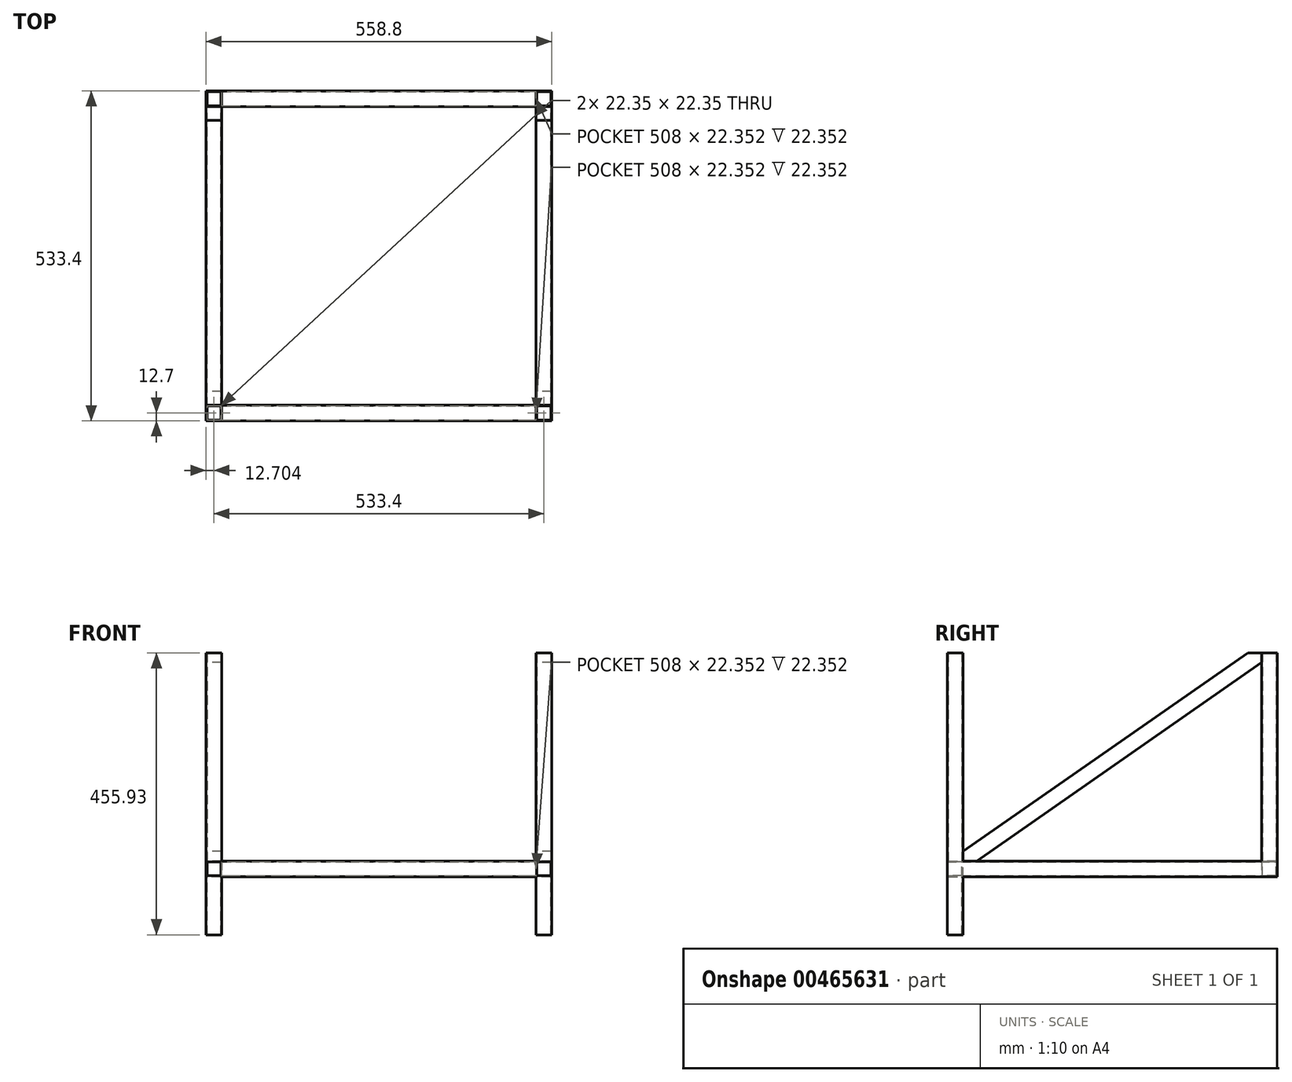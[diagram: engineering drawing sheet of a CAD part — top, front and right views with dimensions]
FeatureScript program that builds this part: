
annotation { "Feature Type Name" : "Feature", "Feature Type Description" : "" }
export const myFeature = defineFeature(function(context is Context, id is Id, definition is map)
    precondition{}
    {
        {
            var Q0;
            Q0=qCreatedBy(makeId("Front.planeOp"),FACE);
            var sketch = newSketch(context, id + "F0", { "sketchPlane" : qUnion([Q0])});
            skLineSegment(sketch, "E0.bottom", {"start": v(20.7, 52.67) * mm, "end": v(46.1, 52.67) * mm});
            skLineSegment(sketch, "E0.top", {"start": v(20.7, 27.27) * mm, "end": v(46.1, 27.27) * mm});
            skLineSegment(sketch, "E0.left", {"start": v(20.7, 52.67) * mm, "end": v(20.7, 27.27) * mm});
            skLineSegment(sketch, "E0.right", {"start": v(46.1, 52.67) * mm, "end": v(46.1, 27.27) * mm});
            skLineSegment(sketch, "E1.bottom", {"start": v(44.58, 28.8) * mm, "end": v(22.23, 28.8) * mm});
            skLineSegment(sketch, "E1.top", {"start": v(44.58, 51.15) * mm, "end": v(22.23, 51.15) * mm});
            skLineSegment(sketch, "E1.left", {"start": v(44.58, 28.8) * mm, "end": v(44.58, 51.15) * mm});
            skLineSegment(sketch, "E1.right", {"start": v(22.23, 28.8) * mm, "end": v(22.23, 51.15) * mm});
            skSolve(sketch);
        }
        {
            var Q0;
            Q0=makeQuery(id+"F0.imprint","IMPRINT",FACE,{"disambiguationData":[TD([[makeQuery(id+"F0.imprint","IMPRINT",EDGE,{"derivedFrom":sQuery(id+"F0.wireOp",EDGE,"E0.bottom")}),-1.0]])]});
            extrude(context, id + "F1", {"entities" : qUnion([Q0]), "depth" : 533.4 * mm});
        }
        {
            var Q0;
            Q0=makeQuery(id+"F1.opExtrude","SWEPT_BODY",BODY,{"disambiguationData":[OSD([sQuery(id+"F0.wireOp",EDGE,"E0.bottom"),sQuery(id+"F0.wireOp",EDGE,"E0.top"),sQuery(id+"F0.wireOp",EDGE,"E0.left"),sQuery(id+"F0.wireOp",EDGE,"E0.right"),sQuery(id+"F0.wireOp",EDGE,"E1.bottom"),sQuery(id+"F0.wireOp",EDGE,"E1.top"),sQuery(id+"F0.wireOp",EDGE,"E1.left"),sQuery(id+"F0.wireOp",EDGE,"E1.right")])]});
            transform(context, id + "F2", {"entities" : qUnion([Q0]), "transformType" : TransformType.TRANSLATION_3D, "dx" : 533.4 * mm, "dy" : 0 * mm, "dz" : 0 * mm, "makeCopy" : true});
        }
        {
            var Q0;
            Q0=makeQuery(id+"F2.opPattern","COPY",FACE,{"derivedFrom":makeQuery(id+"F1.opExtrude","SWEPT_FACE",FACE,{"disambiguationData":[OSD([sQuery(id+"F0.wireOp",EDGE,"E0.left")])]}),"instanceName":"1"});
            var sketch = newSketch(context, id + "F3", { "sketchPlane" : qUnion([Q0])});
            skLineSegment(sketch, "E2.bottom", {"start": v(508, 27.27) * mm, "end": v(533.4, 27.27) * mm});
            skLineSegment(sketch, "E2.top", {"start": v(508, 52.67) * mm, "end": v(533.4, 52.67) * mm});
            skLineSegment(sketch, "E2.left", {"start": v(508, 27.27) * mm, "end": v(508, 52.67) * mm});
            skLineSegment(sketch, "E2.right", {"start": v(533.4, 27.27) * mm, "end": v(533.4, 52.67) * mm});
            skLineSegment(sketch, "E3.bottom", {"start": v(509.52, 28.8) * mm, "end": v(531.88, 28.8) * mm});
            skLineSegment(sketch, "E3.top", {"start": v(509.52, 51.15) * mm, "end": v(531.88, 51.15) * mm});
            skLineSegment(sketch, "E3.left", {"start": v(509.52, 28.8) * mm, "end": v(509.52, 51.15) * mm});
            skLineSegment(sketch, "E3.right", {"start": v(531.88, 28.8) * mm, "end": v(531.88, 51.15) * mm});
            skSolve(sketch);
        }
        {
            var Q0;
            Q0=makeQuery(id+"F3.imprint","IMPRINT",FACE,{"disambiguationData":[TD([[makeQuery(id+"F3.imprint","IMPRINT",EDGE,{"derivedFrom":sQuery(id+"F3.wireOp",EDGE,"E2.bottom")}),-1.0]])]});
            extrude(context, id + "F4", {"entities" : qUnion([Q0]), "depth" : 508 * mm});
        }
        {
            var Q0;
            Q0=makeQuery(id+"F4.opExtrude","SWEPT_BODY",BODY,{"disambiguationData":[OSD([sQuery(id+"F3.wireOp",EDGE,"E2.bottom"),sQuery(id+"F3.wireOp",EDGE,"E2.top"),sQuery(id+"F3.wireOp",EDGE,"E2.left"),sQuery(id+"F3.wireOp",EDGE,"E2.right"),sQuery(id+"F3.wireOp",EDGE,"E3.bottom"),sQuery(id+"F3.wireOp",EDGE,"E3.top"),sQuery(id+"F3.wireOp",EDGE,"E3.left"),sQuery(id+"F3.wireOp",EDGE,"E3.right")])]});
            transform(context, id + "F5", {"entities" : qUnion([Q0]), "transformType" : TransformType.TRANSLATION_3D, "dx" : 0 * mm, "dy" : 508 * mm, "dz" : 0 * mm, "makeCopy" : true});
        }
        {
            var Q0;
            Q0=makeQuery(id+"F1.opExtrude","SWEPT_FACE",FACE,{"disambiguationData":[OSD([sQuery(id+"F0.wireOp",EDGE,"E0.bottom")])]});
            var sketch = newSketch(context, id + "F6", { "sketchPlane" : qUnion([Q0])});
            skLineSegment(sketch, "E4.bottom", {"start": v(46.1, -508) * mm, "end": v(20.7, -508) * mm});
            skLineSegment(sketch, "E4.top", {"start": v(46.1, -533.4) * mm, "end": v(20.7, -533.4) * mm});
            skLineSegment(sketch, "E4.left", {"start": v(46.1, -508) * mm, "end": v(46.1, -533.4) * mm});
            skLineSegment(sketch, "E4.right", {"start": v(20.7, -508) * mm, "end": v(20.7, -533.4) * mm});
            skLineSegment(sketch, "E5.bottom", {"start": v(22.23, -531.88) * mm, "end": v(44.58, -531.88) * mm});
            skLineSegment(sketch, "E5.top", {"start": v(22.23, -509.52) * mm, "end": v(44.58, -509.52) * mm});
            skLineSegment(sketch, "E5.left", {"start": v(22.23, -531.88) * mm, "end": v(22.23, -509.52) * mm});
            skLineSegment(sketch, "E5.right", {"start": v(44.58, -531.88) * mm, "end": v(44.58, -509.52) * mm});
            skSolve(sketch);
        }
        {
            var Q0;
            Q0=makeQuery(id+"F6.imprint","IMPRINT",FACE,{"disambiguationData":[TD([[makeQuery(id+"F6.imprint","IMPRINT",EDGE,{"derivedFrom":sQuery(id+"F6.wireOp",EDGE,"E4.bottom")}),1.0]])]});
            extrude(context, id + "F7", {"entities" : qUnion([Q0]), "operationType" : NewBodyOperationType.ADD, "depth" : 336.55 * mm});
        }
        {
            var Q0;
            Q0=makeQuery(id+"F2.opPattern","COPY",FACE,{"derivedFrom":makeQuery(id+"F1.opExtrude","SWEPT_FACE",FACE,{"disambiguationData":[OSD([sQuery(id+"F0.wireOp",EDGE,"E0.bottom")])]}),"instanceName":"1"});
            var sketch = newSketch(context, id + "F8", { "sketchPlane" : qUnion([Q0])});
            skLineSegment(sketch, "E6.bottom", {"start": v(579.5, -508) * mm, "end": v(554.1, -508) * mm});
            skLineSegment(sketch, "E6.top", {"start": v(579.5, -533.4) * mm, "end": v(554.1, -533.4) * mm});
            skLineSegment(sketch, "E6.left", {"start": v(579.5, -508) * mm, "end": v(579.5, -533.4) * mm});
            skLineSegment(sketch, "E6.right", {"start": v(554.1, -508) * mm, "end": v(554.1, -533.4) * mm});
            skLineSegment(sketch, "E7.bottom", {"start": v(577.98, -509.52) * mm, "end": v(555.63, -509.52) * mm});
            skLineSegment(sketch, "E7.top", {"start": v(577.98, -531.88) * mm, "end": v(555.63, -531.88) * mm});
            skLineSegment(sketch, "E7.left", {"start": v(577.98, -509.52) * mm, "end": v(577.98, -531.88) * mm});
            skLineSegment(sketch, "E7.right", {"start": v(555.63, -509.52) * mm, "end": v(555.63, -531.88) * mm});
            skSolve(sketch);
        }
        {
            var Q0;
            Q0=makeQuery(id+"F8.imprint","IMPRINT",FACE,{"disambiguationData":[TD([[makeQuery(id+"F8.imprint","IMPRINT",EDGE,{"derivedFrom":sQuery(id+"F8.wireOp",EDGE,"E6.bottom")}),1.0]])]});
            extrude(context, id + "F9", {"entities" : qUnion([Q0]), "operationType" : NewBodyOperationType.ADD, "depth" : 336.55 * mm});
        }
        {
            var Q0;
            {var subQ1=sQuery(id+"F0.wireOp",EDGE,"E0.left");var subQ2=sQuery(id+"F0.wireOp",EDGE,"E0.bottom");Q0=makeQuery(id+"F9.boolean.opBoolean","SPLIT",FACE,{"disambiguationData":[TD([makeQuery(id+"F2.opPattern","COPY",FACE,{"derivedFrom":makeQuery(id+"F1.opExtrude","SWEPT_FACE",FACE,{"disambiguationData":[OSD([subQ1])]}),"instanceName":"1"})])],"derivedFrom":makeQuery(id+"F2.opPattern","COPY",FACE,{"derivedFrom":makeQuery(id+"F1.opExtrude","SWEPT_FACE",FACE,{"disambiguationData":[OSD([subQ2])]}),"instanceName":"1"})});}
            var sketch = newSketch(context, id + "F10", { "sketchPlane" : qUnion([Q0])});
            skLineSegment(sketch, "E8.bottom", {"start": v(579.5, 0) * mm, "end": v(554.1, 0) * mm});
            skLineSegment(sketch, "E8.top", {"start": v(579.5, -25.4) * mm, "end": v(554.1, -25.4) * mm});
            skLineSegment(sketch, "E8.left", {"start": v(579.5, 0) * mm, "end": v(579.5, -25.4) * mm});
            skLineSegment(sketch, "E8.right", {"start": v(554.1, 0) * mm, "end": v(554.1, -25.4) * mm});
            skLineSegment(sketch, "E9.bottom", {"start": v(577.98, -1.52) * mm, "end": v(555.63, -1.52) * mm});
            skLineSegment(sketch, "E9.top", {"start": v(577.98, -23.88) * mm, "end": v(555.63, -23.88) * mm});
            skLineSegment(sketch, "E9.left", {"start": v(577.98, -1.52) * mm, "end": v(577.98, -23.88) * mm});
            skLineSegment(sketch, "E9.right", {"start": v(555.63, -1.52) * mm, "end": v(555.63, -23.88) * mm});
            skSolve(sketch);
        }
        {
            var Q0;
            Q0=makeQuery(id+"F10.imprint","IMPRINT",FACE,{"disambiguationData":[TD([[makeQuery(id+"F10.imprint","IMPRINT",EDGE,{"derivedFrom":sQuery(id+"F10.wireOp",EDGE,"E8.bottom")}),-1.0]])]});
            extrude(context, id + "F11", {"entities" : qUnion([Q0]), "operationType" : NewBodyOperationType.ADD, "depth" : 336.55 * mm});
        }
        {
            var Q0;
            {var subQ1=sQuery(id+"F0.wireOp",EDGE,"E0.left");var subQ2=sQuery(id+"F0.wireOp",EDGE,"E0.bottom");Q0=makeQuery(id+"F7.boolean.opBoolean","SPLIT",FACE,{"disambiguationData":[TD([makeQuery(id+"F1.opExtrude","SWEPT_FACE",FACE,{"disambiguationData":[OSD([subQ1])]})])],"derivedFrom":makeQuery(id+"F1.opExtrude","SWEPT_FACE",FACE,{"disambiguationData":[OSD([subQ2])]})});}
            var sketch = newSketch(context, id + "F12", { "sketchPlane" : qUnion([Q0])});
            skLineSegment(sketch, "E10.bottom", {"start": v(46.1, -25.4) * mm, "end": v(20.7, -25.4) * mm});
            skLineSegment(sketch, "E10.top", {"start": v(46.1, 0) * mm, "end": v(20.7, 0) * mm});
            skLineSegment(sketch, "E10.left", {"start": v(46.1, -25.4) * mm, "end": v(46.1, 0) * mm});
            skLineSegment(sketch, "E10.right", {"start": v(20.7, -25.4) * mm, "end": v(20.7, 0) * mm});
            skLineSegment(sketch, "E11.bottom", {"start": v(44.58, -23.88) * mm, "end": v(22.23, -23.88) * mm});
            skLineSegment(sketch, "E11.top", {"start": v(44.58, -1.52) * mm, "end": v(22.23, -1.52) * mm});
            skLineSegment(sketch, "E11.left", {"start": v(44.58, -23.88) * mm, "end": v(44.58, -1.52) * mm});
            skLineSegment(sketch, "E11.right", {"start": v(22.23, -23.88) * mm, "end": v(22.23, -1.52) * mm});
            skSolve(sketch);
        }
        {
            var Q0;
            Q0=makeQuery(id+"F12.imprint","IMPRINT",FACE,{"disambiguationData":[TD([[makeQuery(id+"F12.imprint","IMPRINT",EDGE,{"derivedFrom":sQuery(id+"F12.wireOp",EDGE,"E10.bottom")}),-1.0]])]});
            extrude(context, id + "F13", {"entities" : qUnion([Q0]), "operationType" : NewBodyOperationType.ADD, "depth" : 336.55 * mm});
        }
        {
            var Q0;
            Q0=makeQuery(id+"F1.opExtrude","SWEPT_FACE",FACE,{"disambiguationData":[OSD([sQuery(id+"F0.wireOp",EDGE,"E0.top")])]});
            var sketch = newSketch(context, id + "F14", { "sketchPlane" : qUnion([Q0])});
            skLineSegment(sketch, "E12.bottom", {"start": v(46.1, 533.4) * mm, "end": v(20.7, 533.4) * mm});
            skLineSegment(sketch, "E12.top", {"start": v(46.1, 508) * mm, "end": v(20.7, 508) * mm});
            skLineSegment(sketch, "E12.left", {"start": v(46.1, 533.4) * mm, "end": v(46.1, 508) * mm});
            skLineSegment(sketch, "E12.right", {"start": v(20.7, 533.4) * mm, "end": v(20.7, 508) * mm});
            skLineSegment(sketch, "E13.bottom", {"start": v(44.58, 531.88) * mm, "end": v(22.23, 531.88) * mm});
            skLineSegment(sketch, "E13.top", {"start": v(44.58, 509.52) * mm, "end": v(22.23, 509.52) * mm});
            skLineSegment(sketch, "E13.left", {"start": v(44.58, 531.88) * mm, "end": v(44.58, 509.52) * mm});
            skLineSegment(sketch, "E13.right", {"start": v(22.23, 531.88) * mm, "end": v(22.23, 509.52) * mm});
            skSolve(sketch);
        }
        {
            var Q0;
            Q0=makeQuery(id+"F14.imprint","IMPRINT",FACE,{"disambiguationData":[TD([[makeQuery(id+"F14.imprint","IMPRINT",EDGE,{"derivedFrom":sQuery(id+"F14.wireOp",EDGE,"E12.bottom")}),-1.0]])]});
            extrude(context, id + "F15", {"entities" : qUnion([Q0]), "operationType" : NewBodyOperationType.ADD, "depth" : 93.98 * mm});
        }
        {
            var Q0;
            Q0=makeQuery(id+"F2.opPattern","COPY",FACE,{"derivedFrom":makeQuery(id+"F1.opExtrude","SWEPT_FACE",FACE,{"disambiguationData":[OSD([sQuery(id+"F0.wireOp",EDGE,"E0.top")])]}),"instanceName":"1"});
            var sketch = newSketch(context, id + "F16", { "sketchPlane" : qUnion([Q0])});
            skLineSegment(sketch, "E14.bottom", {"start": v(579.5, 533.4) * mm, "end": v(554.1, 533.4) * mm});
            skLineSegment(sketch, "E14.top", {"start": v(579.5, 508) * mm, "end": v(554.1, 508) * mm});
            skLineSegment(sketch, "E14.left", {"start": v(579.5, 533.4) * mm, "end": v(579.5, 508) * mm});
            skLineSegment(sketch, "E14.right", {"start": v(554.1, 533.4) * mm, "end": v(554.1, 508) * mm});
            skLineSegment(sketch, "E15.bottom", {"start": v(577.98, 531.88) * mm, "end": v(555.63, 531.88) * mm});
            skLineSegment(sketch, "E15.top", {"start": v(577.98, 509.52) * mm, "end": v(555.63, 509.52) * mm});
            skLineSegment(sketch, "E15.left", {"start": v(577.98, 531.88) * mm, "end": v(577.98, 509.52) * mm});
            skLineSegment(sketch, "E15.right", {"start": v(555.63, 531.88) * mm, "end": v(555.63, 509.52) * mm});
            skSolve(sketch);
        }
        {
            var Q0;
            Q0=makeQuery(id+"F16.imprint","IMPRINT",FACE,{"disambiguationData":[TD([[makeQuery(id+"F16.imprint","IMPRINT",EDGE,{"derivedFrom":sQuery(id+"F16.wireOp",EDGE,"E14.bottom")}),-1.0]])]});
            extrude(context, id + "F17", {"entities" : qUnion([Q0]), "operationType" : NewBodyOperationType.ADD, "depth" : 93.98 * mm});
        }
        {
            var Q0;
            Q0=makeQuery(id+"F15.boolean.opBoolean","MERGE",FACE,{"derivedFrom":[makeQuery(id+"F13.boolean.opBoolean","MERGE",FACE,{"derivedFrom":[makeQuery(id+"F7.boolean.opBoolean","MERGE",FACE,{"derivedFrom":[makeQuery(id+"F1.opExtrude","SWEPT_FACE",FACE,{"disambiguationData":[OSD([sQuery(id+"F0.wireOp",EDGE,"E0.left")])]}),makeQuery(id+"F7.opExtrude","SWEPT_FACE",FACE,{"disambiguationData":[OSD([sQuery(id+"F6.wireOp",EDGE,"E4.right")])]})]}),makeQuery(id+"F13.opExtrude","SWEPT_FACE",FACE,{"disambiguationData":[OSD([sQuery(id+"F12.wireOp",EDGE,"E10.right")])]})]}),makeQuery(id+"F15.opExtrude","SWEPT_FACE",FACE,{"disambiguationData":[OSD([sQuery(id+"F14.wireOp",EDGE,"E12.right")])]})]});
            var sketch = newSketch(context, id + "F18", { "sketchPlane" : qUnion([Q0])});
            skLineSegment(sketch, "E16.1", {"start": v(25.4, 52.67) * mm, "end": v(25.4, 389.22) * mm});
            skLineSegment(sketch, "E16.2", {"start": v(25.4, 389.22) * mm, "end": v(508, 389.22) * mm});
            skPoint(sketch, "E16.0.midPoint", {"position": v(266.7, 220.95) * mm});
            skLineSegment(sketch, "E17", {"start": v(508, 371.16) * mm, "end": v(508, 389.22) * mm});
            skLineSegment(sketch, "E18.2", {"start": v(508, 52.67) * mm, "end": v(25.4, 52.67) * mm});
            skPoint(sketch, "E18.0.midPoint", {"position": v(25.4, 220.95) * mm});
            skLineSegment(sketch, "E19.1", {"start": v(47.6, 389.22) * mm, "end": v(508, 68.15) * mm});
            skLineSegment(sketch, "E20.1", {"start": v(25.4, 373.74) * mm, "end": v(485.8, 52.67) * mm});
            skPoint(sketch, "E21.0.midPoint", {"position": v(256.51, 228.05) * mm});
            skSolve(sketch);
        }
        {
            var Q0;
            {var subQ0=sQuery(id+"F18.wireOp",EDGE,"E19.1");Q0=makeQuery(id+"F18.imprint","IMPRINT",FACE,{"disambiguationData":[TD([[makeQuery(id+"F18.imprint","IMPRINT",EDGE,{"derivedFrom":subQ0}),-1.0]])]});}
            extrude(context, id + "F19", {"entities" : qUnion([Q0]), "oppositeDirection" : true, "depth" : 25.4 * mm, "offsetDistance" : 25.4 * mm});
        }
        {
            var Q0;
            Q0=makeQuery(id+"F19.opExtrude","SWEPT_BODY",BODY,{"disambiguationData":[OSD([sQuery(id+"F0.wireOp",EDGE,"E0.bottom"),sQuery(id+"F0.wireOp",EDGE,"E0.left"),sQuery(id+"F6.wireOp",EDGE,"E4.bottom"),sQuery(id+"F6.wireOp",EDGE,"E4.right"),sQuery(id+"F18.wireOp",EDGE,"E16.2"),sQuery(id+"F18.wireOp",EDGE,"87a87b5d-b901-46db-8a5b-8d62eb23e8b0.0"),sQuery(id+"F18.wireOp",EDGE,"2f5da8fb-7c24-4f34-983d-cad889236973.0"),sQuery(id+"F18.wireOp",EDGE,"E17"),sQuery(id+"F18.wireOp",EDGE,"E16.1"),sQuery(id+"F18.wireOp",EDGE,"E18.2"),sQuery(id+"F18.wireOp",EDGE,"E19.1"),sQuery(id+"F18.wireOp",EDGE,"E20.1")])]});
            transform(context, id + "F20", {"entities" : qUnion([Q0]), "transformType" : TransformType.TRANSLATION_3D, "dx" : 533.4 * mm, "dy" : 0 * mm, "dz" : 0 * mm, "makeCopy" : true});
        }
    });
